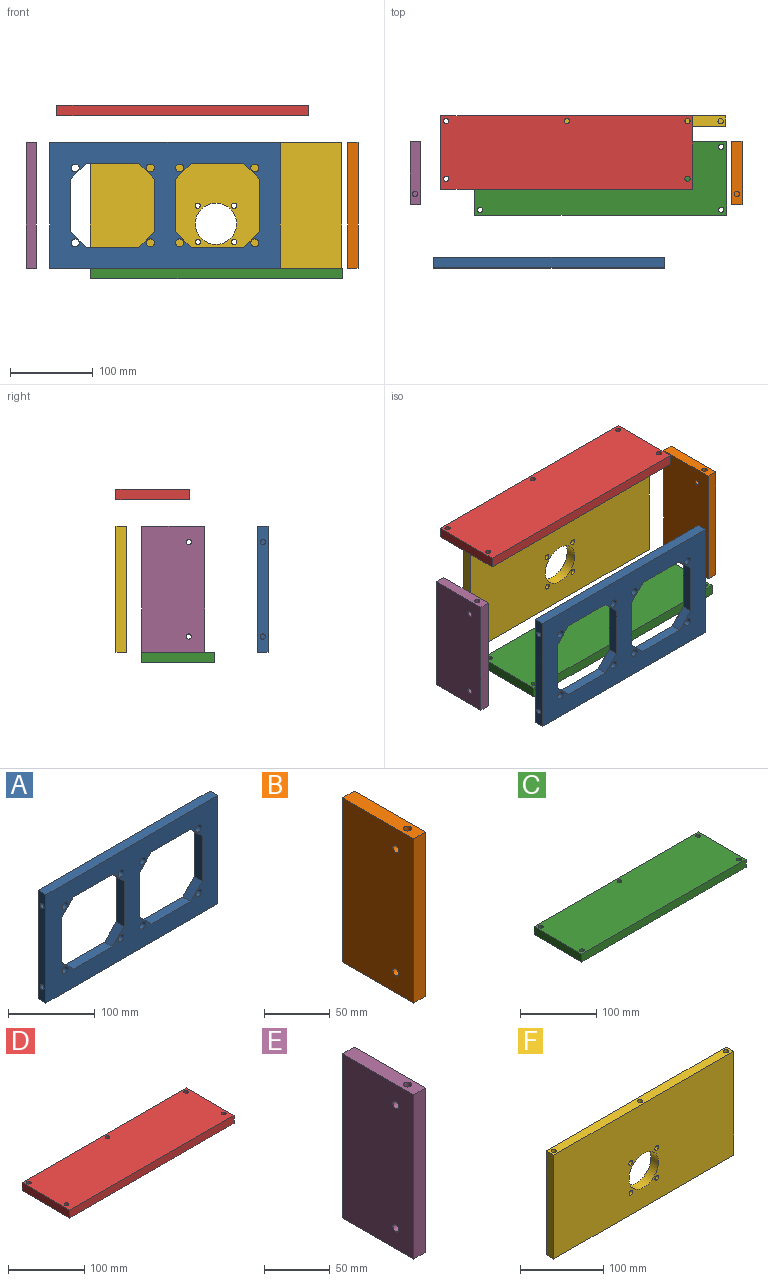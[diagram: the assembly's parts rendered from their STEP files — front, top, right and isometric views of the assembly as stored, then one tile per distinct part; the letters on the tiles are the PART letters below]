
ASSEMBLY  parts=6 mates=5
PART A: 38 faces, bbox 279.4x12.7x152.4 mm
  f0: plane 279.4x152.4mm, normal (0,-1,0), area 22809.2mm2, adj f2,f3,f4,f5,f6,f7,f8,f9
  f1: plane 279.4x152.4mm, normal (0,1,0), area 22809.2mm2, adj f2,f3,f4,f5,f6,f7,f8,f9
  f2: plane 279.4x12.7mm, normal (0,0,1), area 3548.4mm2, adj f0,f1,f3,f12
  f3: plane 152.4x12.7mm, normal (-1,0,0), area 1872.1mm2, adj f0,f1,f2,f4,f34,f36
  f4: plane 279.4x12.7mm, normal (0,0,-1), area 3548.4mm2, adj f0,f1,f3,f12
  f5: cylinder r=4.8mm len=12.7mm, axis (0,1,0), area 382.6mm2, adj f0,f1
  f6: cylinder r=4.8mm len=12.7mm, axis (0,1,0), area 382.6mm2, adj f0,f1
  f7: cylinder r=4.8mm len=12.7mm, axis (0,1,0), area 382.6mm2, adj f0,f1
  f8: cylinder r=4.8mm len=12.7mm, axis (0,1,0), area 382.6mm2, adj f0,f1
  f9: cylinder r=4.8mm len=12.7mm, axis (0,1,0), area 382.6mm2, adj f0,f1
  f10: cylinder r=4.8mm len=12.7mm, axis (0,1,0), area 382.6mm2, adj f0,f1
  f11: cylinder r=4.8mm len=12.7mm, axis (0,1,0), area 382.6mm2, adj f0,f1
  f12: plane 152.4x12.7mm, normal (1,0,0), area 1872.1mm2, adj f0,f1,f2,f4,f30,f32
  f13: cylinder r=4.8mm len=12.7mm, axis (0,1,0), area 382.6mm2, adj f0,f1
  f14: plane 63.5x12.7mm, normal (0,0,-1), area 806.5mm2, adj f0,f1,f15,f21
  f15: plane 19.05x19.05mm, normal (-0.71,0,-0.71), area 342.1mm2, adj f0,f1,f14,f16
  f16: plane 63.5x12.7mm, normal (-1,0,0), area 806.5mm2, adj f0,f1,f15,f17
  f17: plane 19.05x19.05mm, normal (-0.71,0,0.71), area 342.1mm2, adj f0,f1,f16,f18
  f18: plane 63.5x12.7mm, normal (0,0,1), area 806.5mm2, adj f0,f1,f17,f19
  f19: plane 19.05x19.05mm, normal (0.71,0,0.71), area 342.1mm2, adj f0,f1,f18,f20
  f20: plane 63.5x12.7mm, normal (1,0,0), area 806.5mm2, adj f0,f1,f19,f21
  f21: plane 19.05x19.05mm, normal (0.71,0,-0.71), area 342.1mm2, adj f0,f1,f14,f20
  f22: plane 63.5x12.7mm, normal (1,0,0), area 806.5mm2, adj f0,f1,f23,f29
  f23: plane 19.05x19.05mm, normal (0.71,0,0.71), area 342.1mm2, adj f0,f1,f22,f24
  f24: plane 63.5x12.7mm, normal (0,0,1), area 806.5mm2, adj f0,f1,f23,f25
  f25: plane 19.05x19.05mm, normal (-0.71,0,0.71), area 342.1mm2, adj f0,f1,f24,f26
  f26: plane 63.5x12.7mm, normal (-1,0,0), area 806.5mm2, adj f0,f1,f25,f27
  f27: plane 19.05x19.05mm, normal (-0.71,0,-0.71), area 342.1mm2, adj f0,f1,f26,f28
  f28: plane 63.5x12.7mm, normal (0,0,-1), area 806.5mm2, adj f0,f1,f27,f29
  f29: plane 19.05x19.05mm, normal (0.71,0,-0.71), area 342.1mm2, adj f0,f1,f22,f28
  f30: cylinder r=3.17mm len=12.7mm, axis (1,0,0), area 253.4mm2, adj f12,f31
  f31: plane 6.35x6.35mm, normal (1,0,0), area 31.7mm2, adj f30
  f32: cylinder r=3.17mm len=12.7mm, axis (1,0,0), area 253.4mm2, adj f12,f33
  f33: plane 6.35x6.35mm, normal (1,0,0), area 31.7mm2, adj f32
  f34: cylinder r=3.17mm len=12.7mm, axis (-1,0,0), area 253.4mm2, adj f3,f35
  f35: plane 6.35x6.35mm, normal (-1,0,0), area 31.7mm2, adj f34
  f36: cylinder r=3.17mm len=12.7mm, axis (-1,0,0), area 253.4mm2, adj f3,f37
  f37: plane 6.35x6.35mm, normal (-1,0,0), area 31.7mm2, adj f36
PART B: 12 faces, bbox 12.7x76.2x152.4 mm
  f0: plane 76.2x12.7mm, normal (0,0,1), area 936.1mm2, adj f1,f3,f4,f5,f8
  f1: plane 152.4x12.7mm, normal (0,-1,0), area 1935.5mm2, adj f0,f2,f4,f5
  f2: plane 76.2x12.7mm, normal (0,0,-1), area 936.1mm2, adj f1,f3,f4,f5,f6
  f3: plane 152.4x12.7mm, normal (0,1,0), area 1935.5mm2, adj f0,f2,f4,f5
  f4: plane 152.4x76.2mm, normal (1,0,0), area 11549.5mm2, adj f0,f1,f2,f3,f10,f11
  f5: plane 152.4x76.2mm, normal (-1,0,0), area 11549.5mm2, adj f0,f1,f2,f3,f10,f11
  f6: cylinder r=3.17mm len=12.7mm, axis (0,0,-1), area 253.4mm2, adj f2,f7
  f7: plane 6.35x6.35mm, normal (0,0,-1), area 31.7mm2, adj f6
  f8: cylinder r=3.17mm len=12.7mm, axis (0,0,1), area 253.4mm2, adj f0,f9
  f9: plane 6.35x6.35mm, normal (0,0,1), area 31.7mm2, adj f8
  f10: cylinder r=3.17mm len=12.7mm, axis (1,0,0), area 253.4mm2, adj f4,f5
  f11: cylinder r=3.17mm len=12.7mm, axis (1,0,0), area 253.4mm2, adj f4,f5
PART C: 11 faces, bbox 304.8x88.9x12.7 mm
  f0: plane 304.8x88.9mm, normal (0,0,-1), area 26938.4mm2, adj f2,f3,f4,f5,f6,f7,f8,f9
  f1: plane 304.8x88.9mm, normal (0,0,1), area 26938.4mm2, adj f2,f3,f4,f5,f6,f7,f8,f9
  f2: plane 88.9x12.7mm, normal (-1,0,0), area 1129mm2, adj f0,f1,f3,f5
  f3: plane 304.8x12.7mm, normal (0,1,0), area 3871mm2, adj f0,f1,f2,f4
  f4: plane 88.9x12.7mm, normal (1,0,0), area 1129mm2, adj f0,f1,f3,f5
  f5: plane 304.8x12.7mm, normal (0,-1,0), area 3871mm2, adj f0,f1,f2,f4
  f6: cylinder r=3.17mm len=12.7mm, axis (0,0,-1), area 253.4mm2, adj f0,f1
  f7: cylinder r=3.17mm len=12.7mm, axis (0,0,-1), area 253.4mm2, adj f0,f1
  f8: cylinder r=3.17mm len=12.7mm, axis (0,0,-1), area 253.4mm2, adj f0,f1
  f9: cylinder r=3.17mm len=12.7mm, axis (0,0,-1), area 253.4mm2, adj f0,f1
  f10: cylinder r=3.17mm len=12.7mm, axis (0,0,-1), area 253.4mm2, adj f0,f1
PART D: 11 faces, bbox 304.8x88.9x12.7 mm
  f0: plane 304.8x88.9mm, normal (0,0,1), area 26938.4mm2, adj f2,f3,f4,f5,f6,f7,f8,f9
  f1: plane 304.8x88.9mm, normal (0,0,-1), area 26938.4mm2, adj f2,f3,f4,f5,f6,f7,f8,f9
  f2: plane 88.9x12.7mm, normal (-1,0,0), area 1129mm2, adj f0,f1,f3,f5
  f3: plane 304.8x12.7mm, normal (0,-1,0), area 3871mm2, adj f0,f1,f2,f4
  f4: plane 88.9x12.7mm, normal (1,0,0), area 1129mm2, adj f0,f1,f3,f5
  f5: plane 304.8x12.7mm, normal (0,1,0), area 3871mm2, adj f0,f1,f2,f4
  f6: cylinder r=3.17mm len=12.7mm, axis (0,0,1), area 253.4mm2, adj f0,f1
  f7: cylinder r=3.17mm len=12.7mm, axis (0,0,1), area 253.4mm2, adj f0,f1
  f8: cylinder r=3.17mm len=12.7mm, axis (0,0,1), area 253.4mm2, adj f0,f1
  f9: cylinder r=3.17mm len=12.7mm, axis (0,0,1), area 253.4mm2, adj f0,f1
  f10: cylinder r=3.17mm len=12.7mm, axis (0,0,1), area 253.4mm2, adj f0,f1
PART E: 12 faces, bbox 12.7x76.2x152.4 mm
  f0: plane 76.2x12.7mm, normal (0,0,1), area 936.1mm2, adj f1,f3,f4,f5,f8
  f1: plane 152.4x12.7mm, normal (0,1,0), area 1935.5mm2, adj f0,f2,f4,f5
  f2: plane 76.2x12.7mm, normal (0,0,-1), area 936.1mm2, adj f1,f3,f4,f5,f6
  f3: plane 152.4x12.7mm, normal (0,-1,0), area 1935.5mm2, adj f0,f2,f4,f5
  f4: plane 152.4x76.2mm, normal (-1,0,0), area 11549.5mm2, adj f0,f1,f2,f3,f10,f11
  f5: plane 152.4x76.2mm, normal (1,0,0), area 11549.5mm2, adj f0,f1,f2,f3,f10,f11
  f6: cylinder r=3.17mm len=12.7mm, axis (0,0,-1), area 253.4mm2, adj f2,f7
  f7: plane 6.35x6.35mm, normal (0,0,-1), area 31.7mm2, adj f6
  f8: cylinder r=3.17mm len=12.7mm, axis (0,0,1), area 253.4mm2, adj f0,f9
  f9: plane 6.35x6.35mm, normal (0,0,1), area 31.7mm2, adj f8
  f10: cylinder r=3.17mm len=12.7mm, axis (-1,0,0), area 253.4mm2, adj f4,f5
  f11: cylinder r=3.17mm len=12.7mm, axis (-1,0,0), area 253.4mm2, adj f4,f5
PART F: 23 faces, bbox 304.8x12.7x152.4 mm
  f0: plane 304.8x12.7mm, normal (0,0,1), area 3776mm2, adj f2,f3,f4,f5,f17,f19,f21
  f1: plane 304.8x12.7mm, normal (0,0,-1), area 3776mm2, adj f2,f3,f4,f5,f11,f13,f15
  f2: plane 152.4x12.7mm, normal (1,0,0), area 1935.5mm2, adj f0,f1,f4,f5
  f3: plane 152.4x12.7mm, normal (-1,0,0), area 1935.5mm2, adj f0,f1,f4,f5
  f4: plane 304.8x152.4mm, normal (0,1,0), area 44361.3mm2, adj f0,f1,f2,f3,f6,f7,f8,f9
  f5: plane 304.8x152.4mm, normal (0,-1,0), area 44361.3mm2, adj f0,f1,f2,f3,f6,f7,f8,f9
  f6: cylinder r=3.17mm len=12.7mm, axis (0,1,0), area 253.4mm2, adj f4,f5
  f7: cylinder r=3.17mm len=12.7mm, axis (0,1,0), area 253.4mm2, adj f4,f5
  f8: cylinder r=3.17mm len=12.7mm, axis (0,1,0), area 253.4mm2, adj f4,f5
  f9: cylinder r=3.17mm len=12.7mm, axis (0,1,0), area 253.4mm2, adj f4,f5
  f10: cylinder r=25mm len=50mm, axis (0,1,0), area 1994.9mm2, adj f4,f5
  f11: cylinder r=3.17mm len=12.7mm, axis (0,0,-1), area 253.4mm2, adj f1,f12
  f12: plane 6.35x6.35mm, normal (0,0,-1), area 31.7mm2, adj f11
  f13: cylinder r=3.17mm len=12.7mm, axis (0,0,-1), area 253.4mm2, adj f1,f14
  f14: plane 6.35x6.35mm, normal (0,0,-1), area 31.7mm2, adj f13
  f15: cylinder r=3.17mm len=12.7mm, axis (0,0,-1), area 253.4mm2, adj f1,f16
  f16: plane 6.35x6.35mm, normal (0,0,-1), area 31.7mm2, adj f15
  f17: cylinder r=3.17mm len=12.7mm, axis (0,0,1), area 253.4mm2, adj f0,f18
  f18: plane 6.35x6.35mm, normal (0,0,1), area 31.7mm2, adj f17
  f19: cylinder r=3.17mm len=12.7mm, axis (0,0,1), area 253.4mm2, adj f0,f20
  f20: plane 6.35x6.35mm, normal (0,0,1), area 31.7mm2, adj f19
  f21: cylinder r=3.17mm len=12.7mm, axis (0,0,1), area 253.4mm2, adj f0,f22
  f22: plane 6.35x6.35mm, normal (0,0,1), area 31.7mm2, adj f21
PLACE A t=(89.9,-140.49,88.9)mm
PLACE B t=(171.12,-50.91,88.9)mm
PLACE C t=(152.4,-63.5,88.9)mm
PLACE D t=(111.52,-32.64,121.24)mm
PLACE E t=(74.06,-50.94,88.9)mm
PLACE F t=(151.56,-32.64,88.9)mm
MATE planar C.f1 <-> E.f2  axis (0,0,1) through (0,-44.45,12.7)mm
MATE planar A.f4 <-> C.f1  axis (0,0,-1) through (89.9,-153.19,12.7)mm
MATE planar B.f2 <-> C.f1  axis (0,0,-1) through (323.52,-38.21,12.7)mm
MATE planar D.f5 <-> F.f4  axis (0,1,0) through (111.52,30.86,197.44)mm
MATE planar C.f1 <-> F.f1  axis (0,0,1) through (152.4,0,12.7)mm
